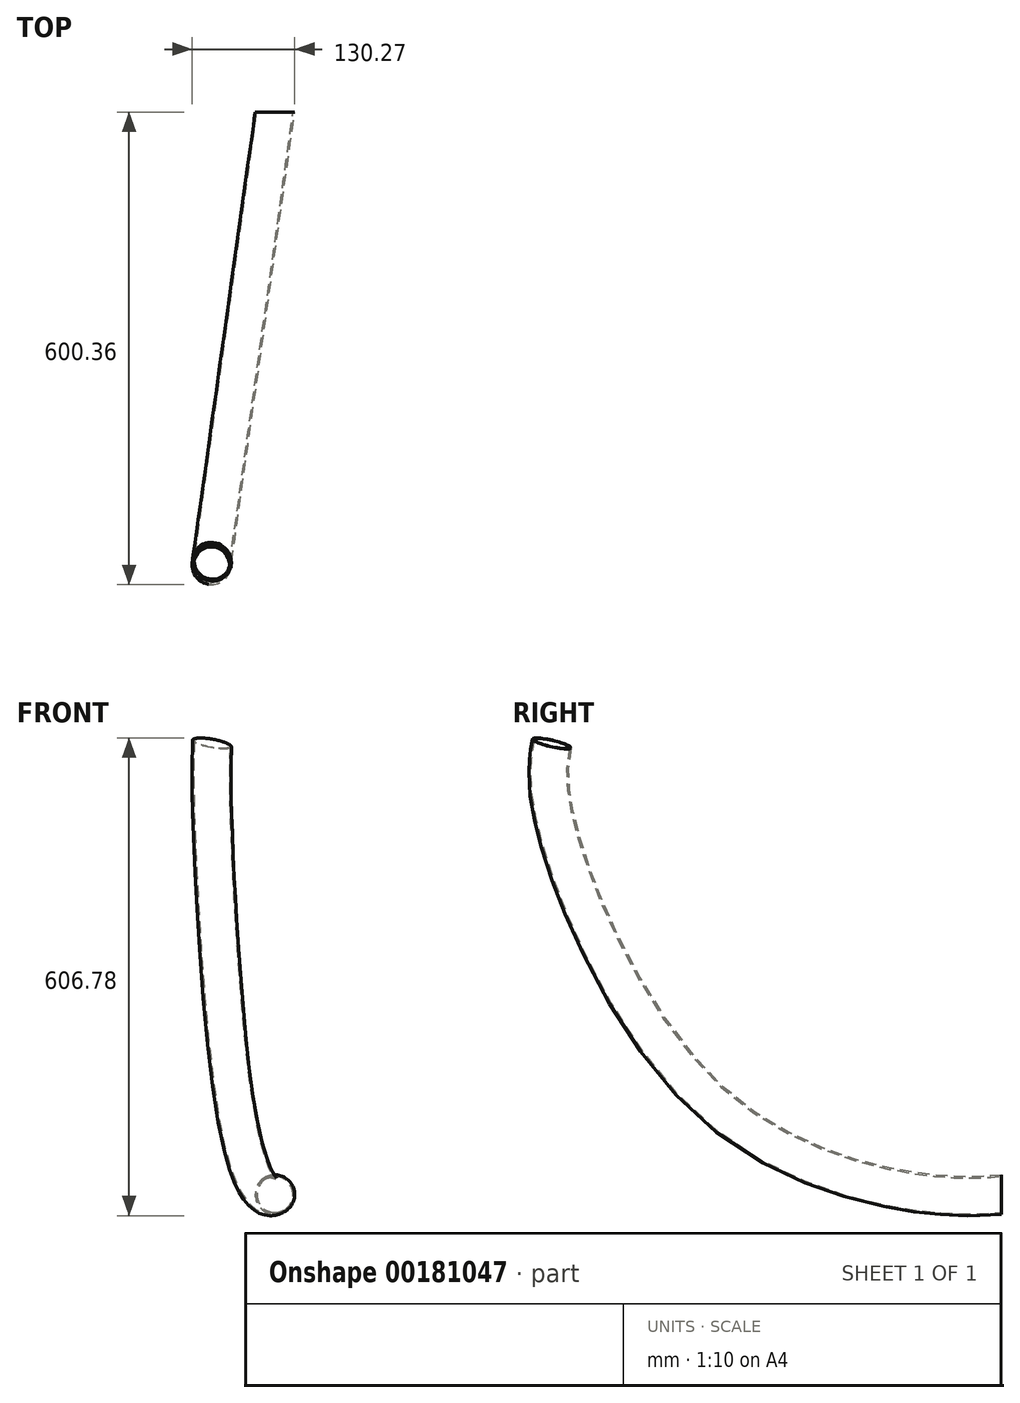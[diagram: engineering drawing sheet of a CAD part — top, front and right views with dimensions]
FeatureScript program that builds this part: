
annotation { "Feature Type Name" : "Feature", "Feature Type Description" : "" }
export const myFeature = defineFeature(function(context is Context, id is Id, definition is map)
    precondition{}
    {
        {
            var Q0;
            Q0=qCreatedBy(makeId("Front.planeOp"),FACE);
            var sketch = newSketch(context, id + "F0", { "sketchPlane" : qUnion([Q0])});
            skPoint(sketch, "E0", {"position": v(0, 0) * mm});
            skPoint(sketch, "E1", {"position": v(79.96, 0) * mm});
            skSolve(sketch);
        }
        {
            var Q0;
            Q0=sQuery(id+"F0.wireOp",VERTEX,"E1");
            var Q1;
            Q1=qCreatedBy(makeId("Right.planeOp"),FACE);
            cPlane(context, id + "F1", {"entities" : qUnion([Q0, Q1]), "cplaneType" : CPlaneType.PLANE_POINT, "offset" : 25 * mm, "width" : 150 * mm, "height" : 150 * mm});
        }
        {
            var Q0;
            Q0=qCreatedBy(id+"F1.planeOp",FACE);
            var sketch = newSketch(context, id + "F2", { "sketchPlane" : qUnion([Q0])});
            skPoint(sketch, "E2.0", {"position": v(0, 0) * mm});
            skPoint(sketch, "E3", {"position": v(571.26, 0) * mm});
            skPoint(sketch, "E4", {"position": v(571.26, -573) * mm});
            skSolve(sketch);
        }
        {
            var Q0;
            Q0=sQuery(id+"F2.wireOp",VERTEX,"E4");
            var Q1;
            Q1=sQuery(id+"F2.wireOp",VERTEX,"E3");
            var Q2;
            Q2=sQuery(id+"F0.wireOp",VERTEX,"E0");
            cPlane(context, id + "F3", {"entities" : qUnion([Q0, Q1, Q2]), "cplaneType" : CPlaneType.THREE_POINT, "offset" : 25 * mm, "width" : 150 * mm, "height" : 150 * mm});
        }
        {
            var Q0;
            Q0=qCreatedBy(id+"F3.planeOp",FACE);
            var sketch = newSketch(context, id + "F4", { "sketchPlane" : qUnion([Q0])});
            skPoint(sketch, "E5.0", {"position": v(0, 0) * mm});
            skPoint(sketch, "E6.0", {"position": v(-576.83, -573) * mm});
            skFitSpline(sketch, "E7", {"points": [v(-576.83, -573) * mm, v(-493.97, -573) * mm, v(-202.93, -454.4) * mm, v(0, -79.93) * mm, v(0, 0) * mm], "startDerivative": vector(428.64, -30.83) * mm, "endDerivative": vector(-68.43, 391.41) * mm});
            skSolve(sketch);
        }
        {
            var Q0;
            Q0=qCreatedBy(makeId("Front.planeOp"),FACE);
            var Q1;
            Q1=sQuery(id+"F4.wireOp",VERTEX,"E6.0");
            cPlane(context, id + "F5", {"entities" : qUnion([Q0, Q1]), "cplaneType" : CPlaneType.PLANE_POINT, "offset" : 25 * mm, "width" : 150 * mm, "height" : 150 * mm});
        }
        {
            var Q0;
            Q0=qCreatedBy(id+"F5.planeOp",FACE);
            var sketch = newSketch(context, id + "F6", { "sketchPlane" : qUnion([Q0])});
            skPoint(sketch, "E8.0", {"position": v(79.96, -573) * mm});
            skCircle(sketch, "E9", {"center": v(79.96, -573) * mm, "radius": 25 * mm});
            skCircle(sketch, "E10.0", {"center": v(79.96, -573) * mm, "radius": 23 * mm});
            skSolve(sketch);
        }
        {
            var Q0;
            Q0=makeQuery(id+"F6.imprint","IMPRINT",FACE,{"disambiguationData":[TD([[makeQuery(id+"F6.imprint","IMPRINT",EDGE,{"derivedFrom":sQuery(id+"F6.wireOp",EDGE,"E9")}),1.0]])]});
            var Q1;
            Q1=sQuery(id+"F4.wireOp",EDGE,"E7");
            sweep(context, id + "F7", {"profiles" : qUnion([Q0]), "path" : qUnion([Q1])});
        }
    });
